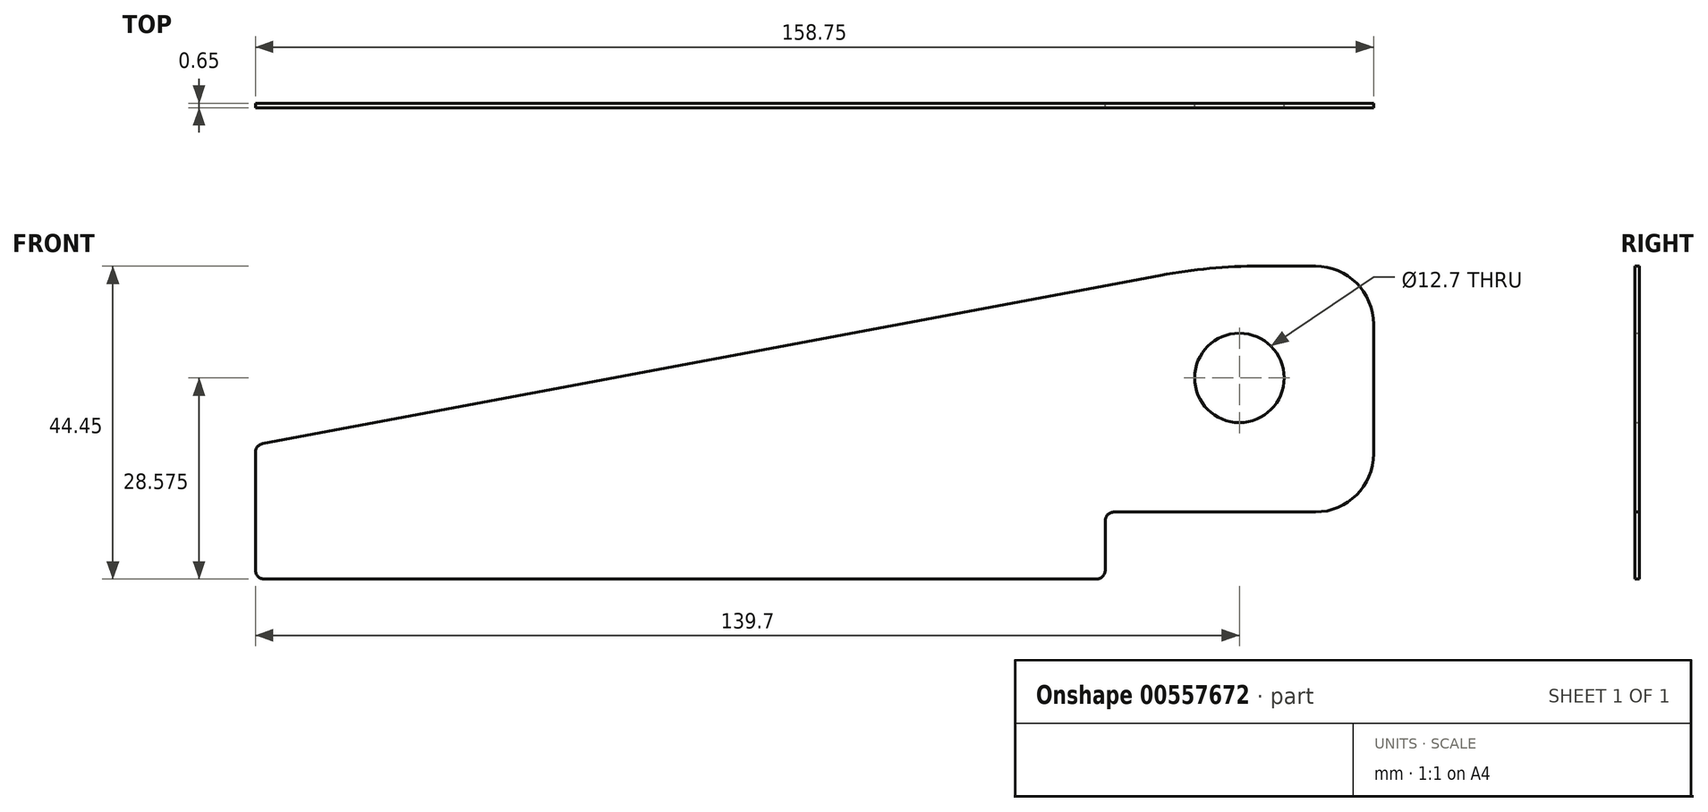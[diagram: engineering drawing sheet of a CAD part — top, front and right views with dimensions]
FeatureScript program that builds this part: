
annotation { "Feature Type Name" : "Feature", "Feature Type Description" : "" }
export const myFeature = defineFeature(function(context is Context, id is Id, definition is map)
    precondition{}
    {
        {
            var Q0;
            Q0=qCreatedBy(makeId("Front.planeOp"),FACE);
            var sketch = newSketch(context, id + "F0", { "sketchPlane" : qUnion([Q0])});
            skLineSegment(sketch, "E0", {"start": v(1.27, 0) * mm, "end": v(119.38, 0) * mm});
            skLineSegment(sketch, "E1", {"start": v(120.65, 1.27) * mm, "end": v(120.65, 8.26) * mm});
            skLineSegment(sketch, "E2", {"start": v(121.92, 9.53) * mm, "end": v(150.5, 9.53) * mm});
            skLineSegment(sketch, "E3", {"start": v(158.75, 17.78) * mm, "end": v(158.75, 36.2) * mm});
            skLineSegment(sketch, "E4", {"start": v(128.5, 43.14) * mm, "end": v(1.04, 19.24) * mm});
            skLineSegment(sketch, "E5", {"start": v(0, 18) * mm, "end": v(0, 1.27) * mm});
            skLineSegment(sketch, "E6", {"start": v(101.6, 38.1) * mm, "end": v(101.6, 0) * mm, "construction": true});
            skPoint(sketch, "E7", {"position": v(139.7, 28.58) * mm});
            skPoint(sketch, "E8.visualSharp", {"position": v(0, 19.05) * mm});
            skArc(sketch, "E8.filletArc", {"start": v(1.04, 19.24) * mm, "mid": v(0.3, 18.8) * mm, "end": v(0, 18) * mm});
            skPoint(sketch, "E9.visualSharp", {"position": v(0, 0) * mm});
            skArc(sketch, "E9.filletArc", {"start": v(0, 1.27) * mm, "mid": v(0.37, 0.37) * mm, "end": v(1.27, 0) * mm});
            skLineSegment(sketch, "E10", {"start": v(142.55, 44.45) * mm, "end": v(150.5, 44.45) * mm});
            skPoint(sketch, "E11.visualSharp", {"position": v(158.75, 44.45) * mm});
            skArc(sketch, "E11.filletArc", {"start": v(158.75, 36.2) * mm, "mid": v(156.33, 42.03) * mm, "end": v(150.5, 44.45) * mm});
            skPoint(sketch, "E12.visualSharp", {"position": v(158.75, 9.53) * mm});
            skArc(sketch, "E12.filletArc", {"start": v(150.5, 9.53) * mm, "mid": v(156.33, 11.94) * mm, "end": v(158.75, 17.78) * mm});
            skPoint(sketch, "E13.visualSharp", {"position": v(120.65, 0) * mm});
            skArc(sketch, "E13.filletArc", {"start": v(119.38, 0) * mm, "mid": v(120.28, 0.37) * mm, "end": v(120.65, 1.27) * mm});
            skPoint(sketch, "E14.visualSharp", {"position": v(120.65, 9.53) * mm});
            skArc(sketch, "E14.filletArc", {"start": v(121.92, 9.53) * mm, "mid": v(121.02, 9.15) * mm, "end": v(120.65, 8.26) * mm});
            skPoint(sketch, "E15.visualSharp", {"position": v(135.47, 44.45) * mm});
            skArc(sketch, "E15.filletArc", {"start": v(142.55, 44.45) * mm, "mid": v(135.5, 44.12) * mm, "end": v(128.5, 43.14) * mm});
            skCircle(sketch, "E16.converted", {"center": v(139.7, 28.58) * mm, "radius": 6.35 * mm});
            skSolve(sketch);
        }
        {
            var Q0;
            Q0=qSketchRegion(id+"F0",true);
            extrude(context, id + "F1", {"entities" : qUnion([Q0]), "depth" : 0.65 * mm, "offsetDistance" : 25.4 * mm});
        }
    });
